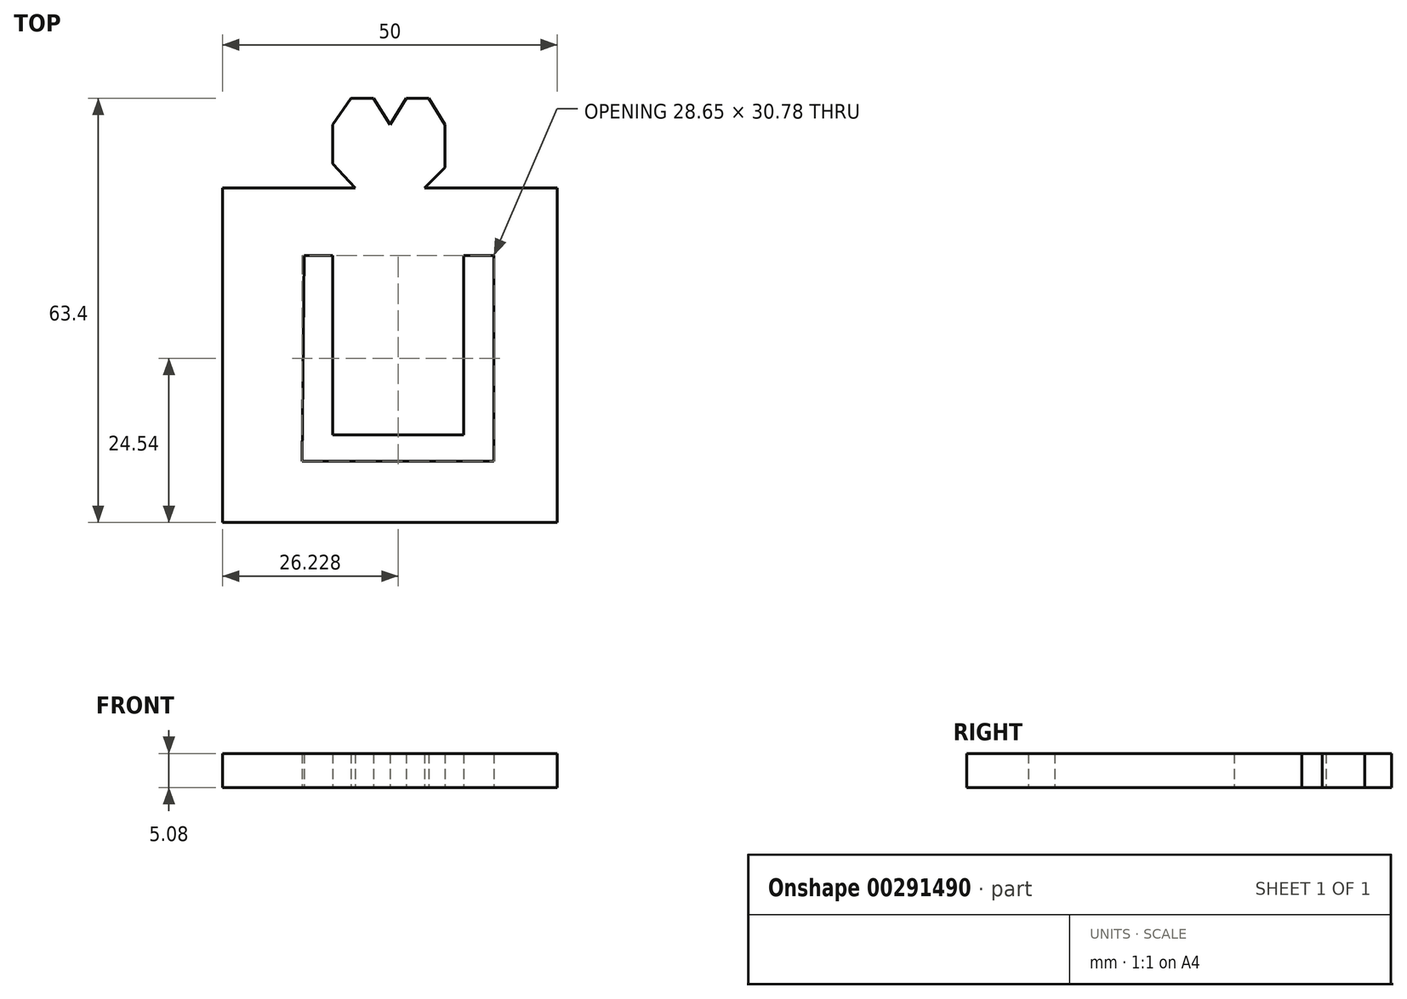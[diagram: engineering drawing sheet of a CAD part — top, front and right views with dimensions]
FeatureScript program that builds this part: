
annotation { "Feature Type Name" : "Feature", "Feature Type Description" : "" }
export const myFeature = defineFeature(function(context is Context, id is Id, definition is map)
    precondition{}
    {
        {
            var Q0;
            Q0=qCreatedBy(makeId("Top.planeOp"),FACE);
            var sketch = newSketch(context, id + "F0", { "sketchPlane" : qUnion([Q0])});
            skLineSegment(sketch, "E0.bottom", {"start": v(-22.57, 17.23) * mm, "end": v(27.43, 17.23) * mm});
            skLineSegment(sketch, "E0.top", {"start": v(-22.57, -32.77) * mm, "end": v(27.43, -32.77) * mm});
            skLineSegment(sketch, "E0.left", {"start": v(-22.57, 17.23) * mm, "end": v(-22.57, -32.77) * mm});
            skLineSegment(sketch, "E0.right", {"start": v(27.43, 17.23) * mm, "end": v(27.43, -32.77) * mm});
            skLineSegment(sketch, "E1", {"start": v(-2.74, 17.23) * mm, "end": v(-6.1, 20.88) * mm});
            skLineSegment(sketch, "E2", {"start": v(-6.1, 20.88) * mm, "end": v(-6.1, 23.62) * mm});
            skLineSegment(sketch, "E3", {"start": v(-6.1, 23.62) * mm, "end": v(-6.1, 26.67) * mm});
            skLineSegment(sketch, "E4", {"start": v(-6.1, 26.67) * mm, "end": v(-3.35, 30.63) * mm});
            skLineSegment(sketch, "E5", {"start": v(-3.35, 30.63) * mm, "end": v(0, 30.63) * mm});
            skLineSegment(sketch, "E6", {"start": v(0, 30.63) * mm, "end": v(2.44, 26.67) * mm});
            skLineSegment(sketch, "E7", {"start": v(2.44, 26.67) * mm, "end": v(4.88, 30.63) * mm});
            skLineSegment(sketch, "E8", {"start": v(4.88, 30.63) * mm, "end": v(8.23, 30.63) * mm});
            skLineSegment(sketch, "E9", {"start": v(8.23, 30.63) * mm, "end": v(10.67, 26.67) * mm});
            skLineSegment(sketch, "E10", {"start": v(10.67, 26.67) * mm, "end": v(10.67, 23.01) * mm});
            skLineSegment(sketch, "E11", {"start": v(10.67, 23.01) * mm, "end": v(10.67, 20.27) * mm});
            skLineSegment(sketch, "E12", {"start": v(10.67, 20.27) * mm, "end": v(7.62, 17.23) * mm});
            skLineSegment(sketch, "E13", {"start": v(-10.36, 7.16) * mm, "end": v(-6.1, 7.16) * mm});
            skLineSegment(sketch, "E14", {"start": v(-6.1, 7.16) * mm, "end": v(-6.1, -19.66) * mm});
            skLineSegment(sketch, "E15", {"start": v(-6.1, -19.66) * mm, "end": v(13.41, -19.66) * mm});
            skLineSegment(sketch, "E16", {"start": v(13.41, -19.66) * mm, "end": v(13.41, 7.16) * mm});
            skLineSegment(sketch, "E17", {"start": v(13.41, 7.16) * mm, "end": v(17.98, 7.16) * mm});
            skLineSegment(sketch, "E18", {"start": v(17.98, 7.16) * mm, "end": v(17.98, -23.62) * mm});
            skLineSegment(sketch, "E19", {"start": v(17.98, -23.62) * mm, "end": v(-10.67, -23.62) * mm});
            skLineSegment(sketch, "E20", {"start": v(-10.67, -23.62) * mm, "end": v(-10.36, 7.16) * mm});
            skLineSegment(sketch, "E21", {"start": v(2.43, 17.23) * mm, "end": v(2.43, -19.66) * mm});
            skLineSegment(sketch, "E22", {"start": v(2.43, -23.62) * mm, "end": v(2.43, -32.77) * mm});
            skLineSegment(sketch, "E23", {"start": v(-22.57, -7.77) * mm, "end": v(-10.51, -7.77) * mm});
            skLineSegment(sketch, "E24", {"start": v(-6.1, -7.77) * mm, "end": v(13.41, -7.77) * mm});
            skPoint(sketch, "E24.startSnap0", {"position": v(-16.54, -7.77) * mm});
            skLineSegment(sketch, "E25", {"start": v(17.98, -7.77) * mm, "end": v(27.43, -7.77) * mm});
            skPoint(sketch, "E25.startSnap0", {"position": v(27.43, -7.77) * mm});
            skSolve(sketch);
        }
        {
            var Q0;
            {var subQ0=sQuery(id+"F0.wireOp",EDGE,"E1");Q0=makeQuery(id+"F0.imprint","IMPRINT",FACE,{"disambiguationData":[TD([[makeQuery(id+"F0.imprint","IMPRINT",EDGE,{"derivedFrom":subQ0}),-1.0]])]});}
            var Q1;
            {var subQ0=sQuery(id+"F0.wireOp",EDGE,"E17");Q1=makeQuery(id+"F0.imprint","IMPRINT",FACE,{"disambiguationData":[TD([[makeQuery(id+"F0.imprint","IMPRINT",EDGE,{"derivedFrom":subQ0}),1.0]])]});}
            var Q2;
            {var subQ3=sQuery(id+"F0.wireOp",EDGE,"E22");Q2=makeQuery(id+"F0.imprint","IMPRINT",FACE,{"disambiguationData":[TD([[makeQuery(id+"F0.imprint","IMPRINT",EDGE,{"derivedFrom":subQ3}),1.0]])]});}
            var Q3;
            {var subQ3=sQuery(id+"F0.wireOp",EDGE,"E22");Q3=makeQuery(id+"F0.imprint","IMPRINT",FACE,{"disambiguationData":[TD([[makeQuery(id+"F0.imprint","IMPRINT",EDGE,{"derivedFrom":subQ3}),-1.0]])]});}
            var Q4;
            {var subQ0=sQuery(id+"F0.wireOp",EDGE,"E13");Q4=makeQuery(id+"F0.imprint","IMPRINT",FACE,{"disambiguationData":[TD([[makeQuery(id+"F0.imprint","IMPRINT",EDGE,{"derivedFrom":subQ0}),1.0]])]});}
            var Q5;
            {var subQ0=sQuery(id+"F0.wireOp",EDGE,"E15");var subQ1=sQuery(id+"F0.wireOp",EDGE,"E14");var subQ2=makeQuery(id+"F0.imprint","INTERSECT",VERTEX,{"derivedFrom":[subQ1,subQ0]});Q5=makeQuery(id+"F0.imprint","IMPRINT",FACE,{"disambiguationData":[TD([[makeQuery(id+"F0.imprint","IMPRINT",EDGE,{"disambiguationData":[TD([[subQ2,1.0]])],"derivedFrom":subQ1}),1.0]])]});}
            var Q6;
            {var subQ0=sQuery(id+"F0.wireOp",EDGE,"E16");var subQ1=sQuery(id+"F0.wireOp",EDGE,"E15");var subQ2=makeQuery(id+"F0.imprint","INTERSECT",VERTEX,{"derivedFrom":[subQ1,subQ0]});Q6=makeQuery(id+"F0.imprint","IMPRINT",FACE,{"disambiguationData":[TD([[makeQuery(id+"F0.imprint","IMPRINT",EDGE,{"disambiguationData":[TD([[subQ2,1.0]])],"derivedFrom":subQ1}),1.0]])]});}
            extrude(context, id + "F1", {"entities" : qUnion([Q0, Q1, Q2, Q3, Q4, Q5, Q6]), "depth" : 5.08 * mm});
        }
    });
